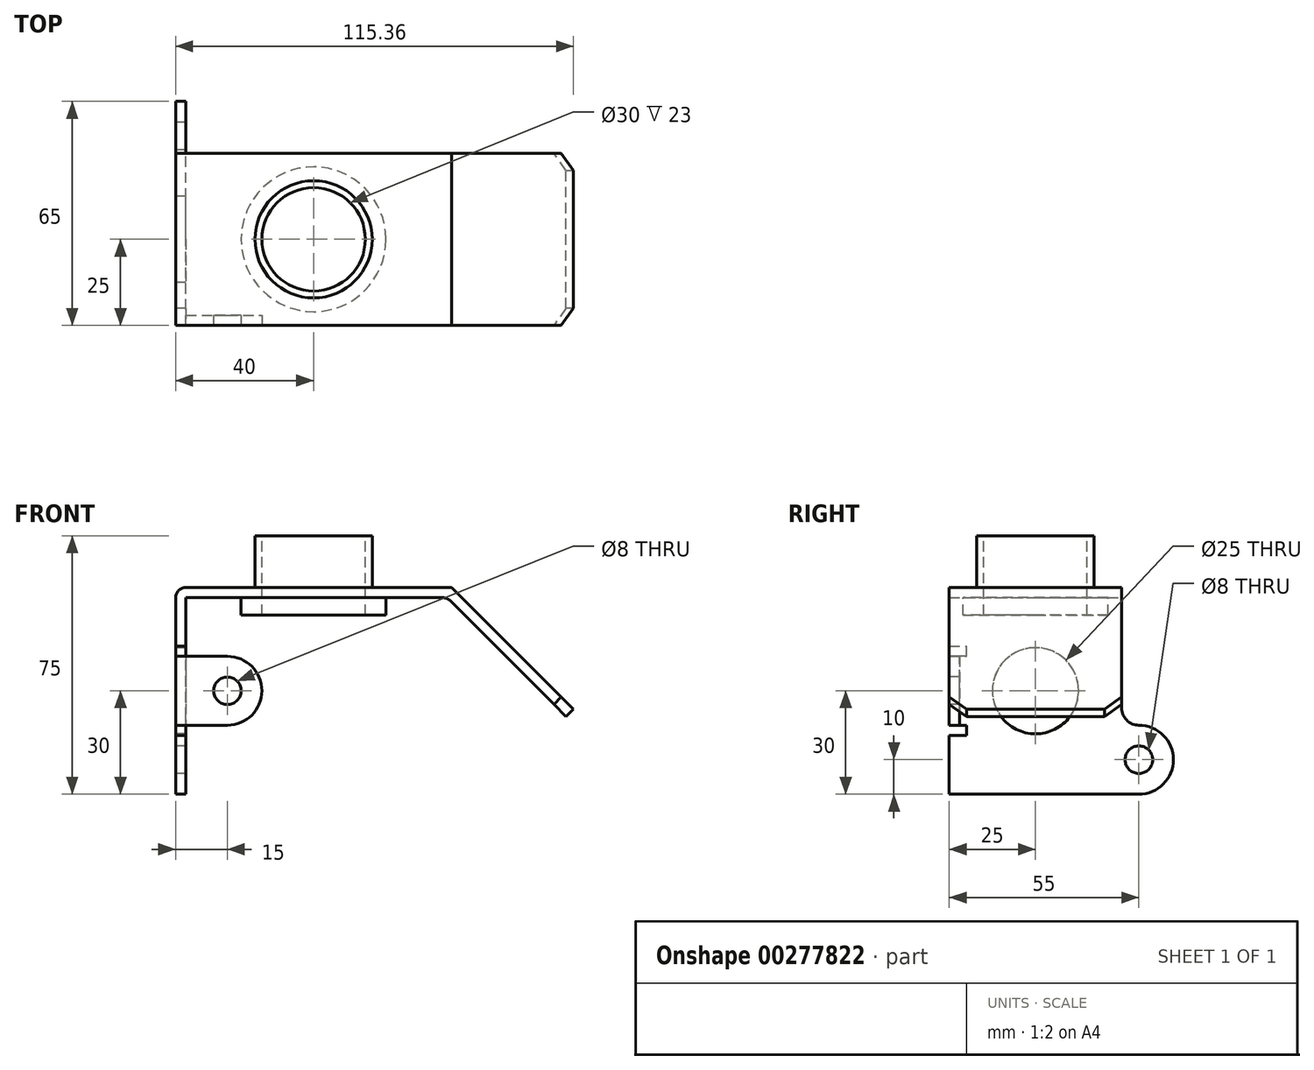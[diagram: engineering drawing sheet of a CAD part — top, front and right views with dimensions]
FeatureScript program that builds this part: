
annotation { "Feature Type Name" : "Feature", "Feature Type Description" : "" }
export const myFeature = defineFeature(function(context is Context, id is Id, definition is map)
    precondition{}
    {
        {
            var Q0;
            Q0=qCreatedBy(makeId("Front.planeOp"),FACE);
            var sketch = newSketch(context, id + "F0", { "sketchPlane" : qUnion([Q0])});
            skLineSegment(sketch, "E0", {"start": v(40, 0) * mm, "end": v(-40, 0) * mm});
            skLineSegment(sketch, "E1", {"start": v(-40, 0) * mm, "end": v(-40, -60) * mm});
            skLineSegment(sketch, "E2", {"start": v(40, 0) * mm, "end": v(75.36, -35.36) * mm});
            skLineSegment(sketch, "E3.0", {"start": v(-37, -3) * mm, "end": v(-37, -60) * mm});
            skLineSegment(sketch, "E4.0", {"start": v(38.76, -3) * mm, "end": v(-37, -3) * mm});
            skLineSegment(sketch, "E5.0", {"start": v(38.76, -3) * mm, "end": v(73.23, -37.48) * mm});
            skLineSegment(sketch, "E6", {"start": v(-40, -60) * mm, "end": v(-37, -60) * mm});
            skLineSegment(sketch, "E7", {"start": v(73.23, -37.48) * mm, "end": v(75.36, -35.36) * mm});
            skSolve(sketch);
        }
        {
            var Q0;
            Q0 = qSketchRegion(id + "F0", true);
            extrude(context, id + "F1", {"entities" : qUnion([Q0]), "depth" : 25 * mm, "hasSecondDirection" : true, "secondDirectionOppositeDirection" : true, "secondDirectionDepth" : 25 * mm});
        }
        {
            var Q0;
            Q0=makeQuery(id+"F1.opExtrude","SWEPT_FACE",FACE,{"disambiguationData":[OSD([sQuery(id+"F0.wireOp",EDGE,"E0")])]});
            var sketch = newSketch(context, id + "F2", { "sketchPlane" : qUnion([Q0])});
            skCircle(sketch, "E8", {"center": v(0, 0) * mm, "radius": 17 * mm});
            skSolve(sketch);
        }
        {
            var Q0;
            Q0=makeQuery(id+"F2.imprint","IMPRINT",FACE,{"disambiguationData":[TD([[makeQuery(id+"F2.imprint","IMPRINT",EDGE,{"derivedFrom":sQuery(id+"F2.wireOp",EDGE,"E8")}),1.0]])]});
            var Q1;
            Q1=sQuery(id+"F2.wireOp",EDGE,"E8");
            extrude(context, id + "F3", {"entities" : qUnion([Q0]), "operationType" : NewBodyOperationType.ADD, "surfaceEntities" : qUnion([Q1]), "depth" : 15 * mm});
        }
        {
            var Q0;
            Q0=makeQuery(id+"F1.opExtrude","SWEPT_FACE",FACE,{"disambiguationData":[OSD([sQuery(id+"F0.wireOp",EDGE,"E4.0")])]});
            var sketch = newSketch(context, id + "F4", { "sketchPlane" : qUnion([Q0])});
            skCircle(sketch, "E9", {"center": v(0, 0) * mm, "radius": 21 * mm});
            skSolve(sketch);
        }
        {
            var Q0;
            Q0=makeQuery(id+"F4.imprint","IMPRINT",FACE,{"disambiguationData":[TD([[makeQuery(id+"F4.imprint","IMPRINT",EDGE,{"derivedFrom":sQuery(id+"F4.wireOp",EDGE,"E9")}),1.0]])]});
            extrude(context, id + "F5", {"entities" : qUnion([Q0]), "operationType" : NewBodyOperationType.ADD, "depth" : 5 * mm});
        }
        {
            var Q0;
            Q0=makeQuery(id+"F3.opExtrude","CAP_FACE",FACE,{"disambiguationData":[OSD([sQuery(id+"F2.wireOp",EDGE,"E8")])],"isStart":false});
            var sketch = newSketch(context, id + "F6", { "sketchPlane" : qUnion([Q0])});
            skPoint(sketch, "E10", {"position": v(0, 0) * mm});
            skSolve(sketch);
        }
        {
            var Q0;
            Q0=sQuery(id+"F6.wireOp",VERTEX,"E10");
            var Q1;
            Q1=makeQuery(id+"F1.opExtrude","SWEPT_BODY",BODY,{"disambiguationData":[OSD([sQuery(id+"F0.wireOp",EDGE,"E0"),sQuery(id+"F0.wireOp",EDGE,"E1"),sQuery(id+"F0.wireOp",EDGE,"E2"),sQuery(id+"F0.wireOp",EDGE,"E3.0"),sQuery(id+"F0.wireOp",EDGE,"E4.0"),sQuery(id+"F0.wireOp",EDGE,"E5.0"),sQuery(id+"F0.wireOp",EDGE,"E6"),sQuery(id+"F0.wireOp",EDGE,"E7")])]});
            hole(context, id + "F7", {"style" : HoleStyle.SIMPLE, "endStyle" : HoleEndStyle.THROUGH, "holeDiameter" : 30 * mm, "tappedDepth" : 12 * mm, "tapClearance" : 3, "locations" : qUnion([Q0]), "scope" : qUnion([Q1])});
        }
        {
            var Q0;
            Q0=makeQuery(id+"F1.opExtrude","SWEPT_FACE",FACE,{"disambiguationData":[OSD([sQuery(id+"F0.wireOp",EDGE,"E1")])]});
            var sketch = newSketch(context, id + "F8", { "sketchPlane" : qUnion([Q0])});
            skLineSegment(sketch, "E11", {"start": v(-41.88, -30) * mm, "end": v(35.8, -30) * mm, "construction": true});
            skLineSegment(sketch, "E12", {"start": v(20, -17) * mm, "end": v(30, -17) * mm});
            skLineSegment(sketch, "E13", {"start": v(30, -43) * mm, "end": v(20, -43) * mm});
            skLineSegment(sketch, "E14", {"start": v(30, -20) * mm, "end": v(20, -20) * mm});
            skLineSegment(sketch, "E15.MirrorCS", {"start": v(30, -40) * mm, "end": v(20, -40) * mm});
            skLineSegment(sketch, "E16", {"start": v(20, -17) * mm, "end": v(20, -20) * mm});
            skLineSegment(sketch, "E17", {"start": v(20, -40) * mm, "end": v(20, -43) * mm});
            skLineSegment(sketch, "E18", {"start": v(30, -17) * mm, "end": v(30, -20) * mm});
            skLineSegment(sketch, "E19", {"start": v(30, -40) * mm, "end": v(30, -43) * mm});
            skPoint(sketch, "E20", {"position": v(0, -30) * mm});
            skPoint(sketch, "E20.positionSnap0", {"position": v(-3.04, -30) * mm});
            skArc(sketch, "E21", {"start": v(-30, -40) * mm, "mid": v(-40, -50) * mm, "end": v(-30, -60) * mm});
            skLineSegment(sketch, "E22", {"start": v(0, -60) * mm, "end": v(-30, -60) * mm});
            skLineSegment(sketch, "E23", {"start": v(-25, -35) * mm, "end": v(-25, -30) * mm});
            skLineSegment(sketch, "E24", {"start": v(-25, -30) * mm, "end": v(0, -30) * mm});
            skLineSegment(sketch, "E25", {"start": v(0, -30) * mm, "end": v(0, -60) * mm});
            skPoint(sketch, "E26.visualSharp", {"position": v(-25, -40) * mm});
            skArc(sketch, "E26.filletArc", {"start": v(-30, -40) * mm, "mid": v(-26.46, -38.54) * mm, "end": v(-25, -35) * mm});
            skSolve(sketch);
        }
        {
            var Q0;
            {var subQ0=sQuery(id+"F8.wireOp",EDGE,"E18");Q0=makeQuery(id+"F8.imprint","IMPRINT",FACE,{"disambiguationData":[TD([[makeQuery(id+"F8.imprint","IMPRINT",EDGE,{"derivedFrom":subQ0}),-1.0]])]});}
            var Q1;
            {var subQ0=sQuery(id+"F8.wireOp",EDGE,"E19");Q1=makeQuery(id+"F8.imprint","IMPRINT",FACE,{"disambiguationData":[TD([[makeQuery(id+"F8.imprint","IMPRINT",EDGE,{"derivedFrom":subQ0}),-1.0]])]});}
            var Q2;
            {var subQ0=sQuery(id+"F8.wireOp",EDGE,"E16");Q2=makeQuery(id+"F8.imprint","IMPRINT",FACE,{"disambiguationData":[TD([[makeQuery(id+"F8.imprint","IMPRINT",EDGE,{"derivedFrom":subQ0}),1.0]])]});}
            var Q3;
            {var subQ0=sQuery(id+"F8.wireOp",EDGE,"E17");Q3=makeQuery(id+"F8.imprint","IMPRINT",FACE,{"disambiguationData":[TD([[makeQuery(id+"F8.imprint","IMPRINT",EDGE,{"derivedFrom":subQ0}),1.0]])]});}
            extrude(context, id + "F9", {"entities" : qUnion([Q0, Q1, Q2, Q3]), "operationType" : NewBodyOperationType.REMOVE, "oppositeDirection" : true, "depth" : 5 * mm});
        }
        {
            var Q0;
            {var subQ0=sQuery(id+"F8.wireOp",EDGE,"E21");Q0=makeQuery(id+"F8.imprint","IMPRINT",FACE,{"disambiguationData":[TD([[makeQuery(id+"F8.imprint","IMPRINT",EDGE,{"derivedFrom":subQ0}),1.0]])]});}
            var Q1;
            {var subQ1=sQuery(id+"F8.wireOp",EDGE,"E23");Q1=makeQuery(id+"F8.imprint","IMPRINT",FACE,{"disambiguationData":[TD([[makeQuery(id+"F8.imprint","IMPRINT",EDGE,{"derivedFrom":subQ1}),1.0]])]});}
            extrude(context, id + "F10", {"entities" : qUnion([Q0, Q1]), "operationType" : NewBodyOperationType.ADD, "oppositeDirection" : true, "depth" : 3 * mm});
        }
        {
            var Q0;
            Q0=sQuery(id+"F8.wireOp",VERTEX,"E20");
            var Q1;
            Q1=makeQuery(id+"F1.opExtrude","SWEPT_BODY",BODY,{"disambiguationData":[OSD([sQuery(id+"F0.wireOp",EDGE,"E0"),sQuery(id+"F0.wireOp",EDGE,"E1"),sQuery(id+"F0.wireOp",EDGE,"E2"),sQuery(id+"F0.wireOp",EDGE,"E3.0"),sQuery(id+"F0.wireOp",EDGE,"E4.0"),sQuery(id+"F0.wireOp",EDGE,"E5.0"),sQuery(id+"F0.wireOp",EDGE,"E6"),sQuery(id+"F0.wireOp",EDGE,"E7")])]});
            hole(context, id + "F11", {"style" : HoleStyle.SIMPLE, "endStyle" : HoleEndStyle.BLIND, "holeDiameter" : 25 * mm, "holeDepth" : 5 * mm, "tappedDepth" : 12 * mm, "tapClearance" : 3, "locations" : qUnion([Q0]), "scope" : qUnion([Q1])});
        }
        {
            var Q0;
            Q0=sQuery(id+"F8.wireOp",VERTEX,"E21.center");
            var Q1;
            Q1=makeQuery(id+"F1.opExtrude","SWEPT_BODY",BODY,{"disambiguationData":[OSD([sQuery(id+"F0.wireOp",EDGE,"E0"),sQuery(id+"F0.wireOp",EDGE,"E1"),sQuery(id+"F0.wireOp",EDGE,"E2"),sQuery(id+"F0.wireOp",EDGE,"E3.0"),sQuery(id+"F0.wireOp",EDGE,"E4.0"),sQuery(id+"F0.wireOp",EDGE,"E5.0"),sQuery(id+"F0.wireOp",EDGE,"E6"),sQuery(id+"F0.wireOp",EDGE,"E7")])]});
            hole(context, id + "F12", {"style" : HoleStyle.SIMPLE, "endStyle" : HoleEndStyle.THROUGH, "holeDiameter" : 8 * mm, "tappedDepth" : 12 * mm, "tapClearance" : 3, "locations" : qUnion([Q0]), "scope" : qUnion([Q1])});
        }
        {
            var Q0;
            {var subQ0=sQuery(id+"F0.wireOp",EDGE,"E1");var subQ1=sQuery(id+"F0.wireOp",EDGE,"E3.0");Q0=makeQuery(id+"F9.boolean.opBoolean","SPLIT",FACE,{"disambiguationData":[TD([makeQuery(id+"F9.opExtrude","SWEPT_FACE",FACE,{"disambiguationData":[OSD([sQuery(id+"F8.wireOp",EDGE,"E15.MirrorCS")])]})])],"derivedFrom":makeQuery(id+"F1.opExtrude","CAP_FACE",FACE,{"disambiguationData":[OSD([sQuery(id+"F0.wireOp",EDGE,"E0"),subQ0,sQuery(id+"F0.wireOp",EDGE,"E2"),subQ1,sQuery(id+"F0.wireOp",EDGE,"E4.0"),sQuery(id+"F0.wireOp",EDGE,"E5.0"),sQuery(id+"F0.wireOp",EDGE,"E6"),sQuery(id+"F0.wireOp",EDGE,"E7")])],"isStart":false})});}
            var sketch = newSketch(context, id + "F13", { "sketchPlane" : qUnion([Q0])});
            skLineSegment(sketch, "E27", {"start": v(-40, -20) * mm, "end": v(-25, -20) * mm});
            skLineSegment(sketch, "E28", {"start": v(-40, -40) * mm, "end": v(-25, -40) * mm});
            skArc(sketch, "E29", {"start": v(-25, -40) * mm, "mid": v(-15, -30) * mm, "end": v(-25, -20) * mm});
            skPoint(sketch, "E30.orphan", {"position": v(-11.1, -20) * mm});
            skPoint(sketch, "E31.orphan", {"position": v(-11.1, -40) * mm});
            skSolve(sketch);
        }
        {
            var Q0;
            {var subQ3=sQuery(id+"F13.wireOp",EDGE,"E29");Q0=makeQuery(id+"F13.imprint","IMPRINT",FACE,{"disambiguationData":[TD([[makeQuery(id+"F13.imprint","IMPRINT",EDGE,{"derivedFrom":subQ3}),1.0]])]});}
            var Q1;
            {var subQ2=sQuery(id+"F0.wireOp",EDGE,"E1");var subQ4=makeQuery(id+"F9.opExtrude","SWEPT_FACE",FACE,{"disambiguationData":[OSD([sQuery(id+"F8.wireOp",EDGE,"E14")])]});var subQ6=makeQuery(id+"F9.boolean.opBoolean","SPLIT",EDGE,{"disambiguationData":[TD([subQ4])],"derivedFrom":makeQuery(id+"F1.opExtrude","CAP_EDGE",EDGE,{"disambiguationData":[OSD([subQ2])],"isStart":false})});Q1=makeQuery(id+"F13.imprint","IMPRINT",FACE,{"disambiguationData":[TD([[makeQuery(id+"F13.imprint","IMPRINT",EDGE,{"derivedFrom":subQ6}),1.0]])]});}
            extrude(context, id + "F14", {"entities" : qUnion([Q0, Q1]), "operationType" : NewBodyOperationType.ADD, "oppositeDirection" : true, "depth" : 3 * mm});
        }
        {
            var Q0;
            {var subQ0=sQuery(id+"F0.wireOp",EDGE,"E1");var subQ1=sQuery(id+"F0.wireOp",EDGE,"E3.0");Q0=makeQuery(id+"F14.boolean.opBoolean","MERGE",FACE,{"derivedFrom":[makeQuery(id+"F9.boolean.opBoolean","SPLIT",FACE,{"disambiguationData":[TD([makeQuery(id+"F9.opExtrude","SWEPT_FACE",FACE,{"disambiguationData":[OSD([sQuery(id+"F8.wireOp",EDGE,"E15.MirrorCS")])]})])],"derivedFrom":makeQuery(id+"F1.opExtrude","CAP_FACE",FACE,{"disambiguationData":[OSD([sQuery(id+"F0.wireOp",EDGE,"E0"),subQ0,sQuery(id+"F0.wireOp",EDGE,"E2"),subQ1,sQuery(id+"F0.wireOp",EDGE,"E4.0"),sQuery(id+"F0.wireOp",EDGE,"E5.0"),sQuery(id+"F0.wireOp",EDGE,"E6"),sQuery(id+"F0.wireOp",EDGE,"E7")])],"isStart":false})}),makeQuery(id+"F14.opExtrude","CAP_FACE",FACE,{"disambiguationData":[OSD([subQ0,sQuery(id+"F13.wireOp",EDGE,"E27"),sQuery(id+"F13.wireOp",EDGE,"E28"),sQuery(id+"F13.wireOp",EDGE,"E29")])],"isStart":true})]});}
            var sketch = newSketch(context, id + "F15", { "sketchPlane" : qUnion([Q0])});
            skPoint(sketch, "E32", {"position": v(-25, -30) * mm});
            skSolve(sketch);
        }
        {
            var Q0;
            Q0=sQuery(id+"F15.wireOp",VERTEX,"E32");
            var Q1;
            Q1=makeQuery(id+"F1.opExtrude","SWEPT_BODY",BODY,{"disambiguationData":[OSD([sQuery(id+"F0.wireOp",EDGE,"E0"),sQuery(id+"F0.wireOp",EDGE,"E1"),sQuery(id+"F0.wireOp",EDGE,"E2"),sQuery(id+"F0.wireOp",EDGE,"E3.0"),sQuery(id+"F0.wireOp",EDGE,"E4.0"),sQuery(id+"F0.wireOp",EDGE,"E5.0"),sQuery(id+"F0.wireOp",EDGE,"E6"),sQuery(id+"F0.wireOp",EDGE,"E7")])]});
            hole(context, id + "F16", {"style" : HoleStyle.SIMPLE, "endStyle" : HoleEndStyle.BLIND, "holeDiameter" : 8 * mm, "holeDepth" : 5 * mm, "tappedDepth" : 12 * mm, "tapClearance" : 3, "locations" : qUnion([Q0]), "scope" : qUnion([Q1])});
        }
        {
            var Q0;
            Q0=makeQuery(id+"F1.opExtrude","SWEPT_FACE",FACE,{"disambiguationData":[OSD([sQuery(id+"F0.wireOp",EDGE,"E2")])]});
            var sketch = newSketch(context, id + "F17", { "sketchPlane" : qUnion([Q0])});
            skLineSegment(sketch, "E33", {"start": v(53.28, -27.55) * mm, "end": v(53.28, 28.96) * mm, "construction": true});
            skPoint(sketch, "E34", {"position": v(38.28, -15) * mm});
            skPoint(sketch, "E35", {"position": v(68.28, -15) * mm});
            skPoint(sketch, "E36", {"position": v(38.28, 15) * mm});
            skPoint(sketch, "E37", {"position": v(68.28, 15) * mm});
            skSolve(sketch);
        }
        {
            var Q0;
            Q0=sQuery(id+"F17.wireOp",VERTEX,"E34");
            var Q1;
            Q1=sQuery(id+"F17.wireOp",VERTEX,"E36");
            var Q2;
            Q2=sQuery(id+"F17.wireOp",VERTEX,"E35");
            var Q3;
            Q3=sQuery(id+"F17.wireOp",VERTEX,"E37");
            var Q4;
            Q4=makeQuery(id+"F1.opExtrude","SWEPT_BODY",BODY,{"disambiguationData":[OSD([sQuery(id+"F0.wireOp",EDGE,"E0"),sQuery(id+"F0.wireOp",EDGE,"E1"),sQuery(id+"F0.wireOp",EDGE,"E2"),sQuery(id+"F0.wireOp",EDGE,"E3.0"),sQuery(id+"F0.wireOp",EDGE,"E4.0"),sQuery(id+"F0.wireOp",EDGE,"E5.0"),sQuery(id+"F0.wireOp",EDGE,"E6"),sQuery(id+"F0.wireOp",EDGE,"E7")])]});
            hole(context, id + "F18", {"style" : HoleStyle.SIMPLE, "endStyle" : HoleEndStyle.BLIND, "holeDiameter" : 8 * mm, "holeDepth" : 5 * mm, "tappedDepth" : 12 * mm, "tapClearance" : 3, "locations" : qUnion([Q0, Q1, Q2, Q3]), "scope" : qUnion([Q4])});
        }
        {
            var Q0;
            Q0=makeQuery(id+"F1.opExtrude","CAP_EDGE",EDGE,{"disambiguationData":[OSD([sQuery(id+"F0.wireOp",EDGE,"E7")])],"isStart":true});
            var Q1;
            Q1=makeQuery(id+"F1.opExtrude","CAP_EDGE",EDGE,{"disambiguationData":[OSD([sQuery(id+"F0.wireOp",EDGE,"E7")])],"isStart":false});
            chamfer(context, id + "F19", {"entities" : qUnion([Q0, Q1]), "width" : 5 * mm, "tangentPropagation" : true});
        }
        {
            var Q0;
            Q0=makeQuery(id+"F1.opExtrude","SWEPT_EDGE",EDGE,{"disambiguationData":[OSD([sQuery(id+"F0.wireOp",EDGE,"E0"),sQuery(id+"F0.wireOp",EDGE,"E1")])]});
            var Q1;
            Q1=makeQuery(id+"F1.opExtrude","SWEPT_EDGE",EDGE,{"disambiguationData":[OSD([sQuery(id+"F0.wireOp",EDGE,"E4.0"),sQuery(id+"F0.wireOp",EDGE,"E5.0")])]});
            fillet(context, id + "F20", {"entities" : qUnion([Q0, Q1]), "radius" : 3 * mm, "tangentPropagation" : true, "allowEdgeOverflow" : false});
        }
    });
